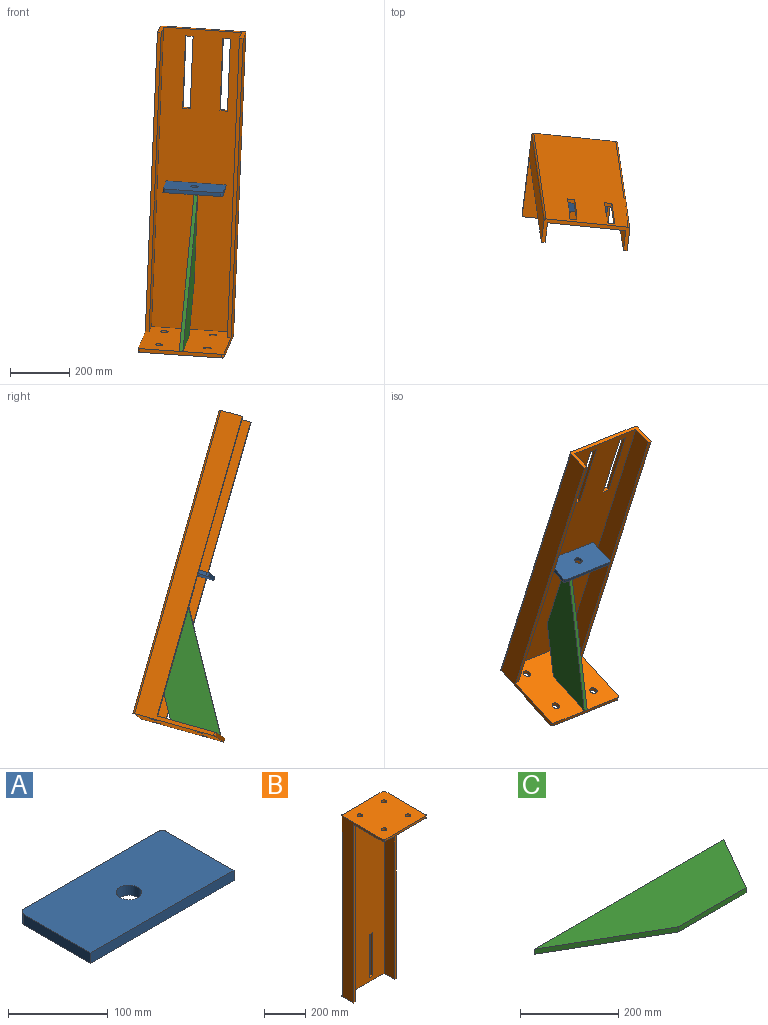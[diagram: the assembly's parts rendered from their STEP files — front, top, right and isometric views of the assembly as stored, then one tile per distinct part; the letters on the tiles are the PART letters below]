
ASSEMBLY  parts=3 mates=2
PART A: 9 faces, bbox 203.2x101.6x12.7 mm
  f0: cylinder r=6.35mm len=12.7mm, axis (0,0,-1), area 126.7mm2, adj f1,f5,f6,f7
  f1: plane 95.25x12.7mm, normal (-1,0,0), area 1209.7mm2, adj f0,f2,f6,f7
  f2: plane 203.2x12.7mm, normal (0,-1,0), area 2580.6mm2, adj f1,f3,f6,f7
  f3: plane 95.25x12.7mm, normal (1,0,0), area 1209.7mm2, adj f2,f4,f6,f7
  f4: cylinder r=6.35mm len=12.7mm, axis (0,0,-1), area 126.7mm2, adj f3,f5,f6,f7
  f5: plane 190.5x12.7mm, normal (0,1,0), area 2419.3mm2, adj f0,f4,f6,f7
  f6: plane 203.2x101.6mm, normal (0,0,1), area 20121.1mm2, adj f0,f1,f2,f3,f4,f5,f8
  f7: plane 203.2x101.6mm, normal (0,0,-1), area 20121.1mm2, adj f0,f1,f2,f3,f4,f5,f8
  f8: cylinder r=12.7mm len=25.4mm, axis (0,0,1), area 1013.4mm2, adj f6,f7
PART B: 28 faces, bbox 292.1x292.1x1066.8 mm
  f0: plane 1054.1x266.7mm, normal (0,-1,0), area 268225.3mm2, adj f4,f5,f10,f11,f20,f21,f22,f23
  f1: plane 1066.8x279.4mm, normal (0,1,0), area 285160.7mm2, adj f8,f9,f10,f15,f20,f21,f22,f23
  f2: plane 1066.8x279.4mm, normal (-1,0,0), area 83870.8mm2, adj f3,f9,f10,f11,f12,f15
  f3: plane 1054.1x12.7mm, normal (0,-1,0), area 13387.1mm2, adj f2,f4,f10,f11
  f4: plane 1054.1x69.85mm, normal (1,0,0), area 73628.9mm2, adj f0,f3,f10,f11
  f5: plane 1054.1x69.85mm, normal (-1,0,0), area 73628.9mm2, adj f0,f6,f10,f11
  f6: plane 1054.1x12.7mm, normal (0,-1,0), area 13387.1mm2, adj f5,f7,f10,f11
  f7: plane 1066.8x279.4mm, normal (1,0,0), area 83870.8mm2, adj f6,f8,f10,f11,f14,f15
  f8: cylinder r=6.35mm len=1066.8mm, axis (0,0,-1), area 10640.9mm2, adj f1,f7,f10,f15
  f9: cylinder r=6.35mm len=1066.8mm, axis (0,0,-1), area 10640.9mm2, adj f1,f2,f10,f15
  f10: plane 292.1x82.55mm, normal (0,0,-1), area 5466.6mm2, adj f0,f1,f2,f3,f4,f5,f6,f7
  f11: plane 292.1x279.4mm, normal (0,0,-1), area 77794.4mm2, adj f0,f2,f3,f4,f5,f6,f7,f12
  f12: cylinder r=6.35mm len=12.7mm, axis (0,0,-1), area 126.7mm2, adj f2,f11,f13,f15
  f13: plane 279.4x12.7mm, normal (0,-1,0), area 3548.4mm2, adj f11,f12,f14,f15
  f14: cylinder r=6.35mm len=12.7mm, axis (0,0,-1), area 126.7mm2, adj f7,f11,f13,f15
  f15: plane 292.1x292.1mm, normal (0,0,1), area 83261mm2, adj f1,f2,f7,f8,f9,f12,f13,f14
  f16: cylinder r=12.7mm len=25.4mm, axis (0,0,1), area 1013.4mm2, adj f11,f15
  f17: cylinder r=12.7mm len=25.4mm, axis (0,0,1), area 1013.4mm2, adj f11,f15
  f18: cylinder r=12.7mm len=25.4mm, axis (0,0,1), area 1013.4mm2, adj f11,f15
  f19: cylinder r=12.7mm len=25.4mm, axis (0,0,1), area 1013.4mm2, adj f11,f15
  f20: plane 25.4x12.7mm, normal (0,0,-1), area 322.6mm2, adj f0,f1,f21,f23
  f21: plane 254x12.7mm, normal (1,0,0), area 3225.8mm2, adj f0,f1,f20,f22
  f22: plane 25.4x12.7mm, normal (0,0,1), area 322.6mm2, adj f0,f1,f21,f23
  f23: plane 254x12.7mm, normal (-1,0,0), area 3225.8mm2, adj f0,f1,f20,f22
  f24: plane 25.4x12.7mm, normal (0,0,-1), area 322.6mm2, adj f0,f1,f25,f27
  f25: plane 254x12.7mm, normal (1,0,0), area 3225.8mm2, adj f0,f1,f24,f26
  f26: plane 25.4x12.7mm, normal (0,0,1), area 322.6mm2, adj f0,f1,f25,f27
  f27: plane 254x12.7mm, normal (-1,0,0), area 3225.8mm2, adj f0,f1,f24,f26
PART C: 6 faces, bbox 546.1x152.4x12.7 mm
  f0: plane 546.1x12.7mm, normal (0,1,0), area 6935.5mm2, adj f1,f3,f4,f5
  f1: plane 263.96x152.4mm, normal (-0.5,-0.87,0), area 3871mm2, adj f0,f2,f4,f5
  f2: plane 194.15x12.7mm, normal (0,-1,0), area 2465.7mm2, adj f1,f3,f4,f5
  f3: plane 152.4x87.99mm, normal (0.87,-0.5,0), area 2234.9mm2, adj f0,f2,f4,f5
  f4: plane 546.1x152.4mm, normal (0,0,1), area 56406.8mm2, adj f0,f1,f2,f3
  f5: plane 546.1x152.4mm, normal (0,0,-1), area 56406.8mm2, adj f0,f1,f2,f3
PLACE A rot(axis=(-1,0.06,0.03),164.3deg) t=(-611.44,395.59,709.92)mm
PLACE B rot(axis=(-0.05,-0.99,-0.14),176.9deg) t=(-525.79,247.98,1224.98)mm
PLACE C rot(axis=(0.67,-0.12,-0.73),173.7deg) t=(-580.03,303.23,83.97)mm
MATE fastened A.f2 <-> B.f0  axis (0.12,0.96,0.27) through (-527.27,462.58,718.95)mm
MATE fastened C.f3 <-> B.f11  axis (-0.04,0.27,-0.96) through (-578.37,334.29,154.94)mm
